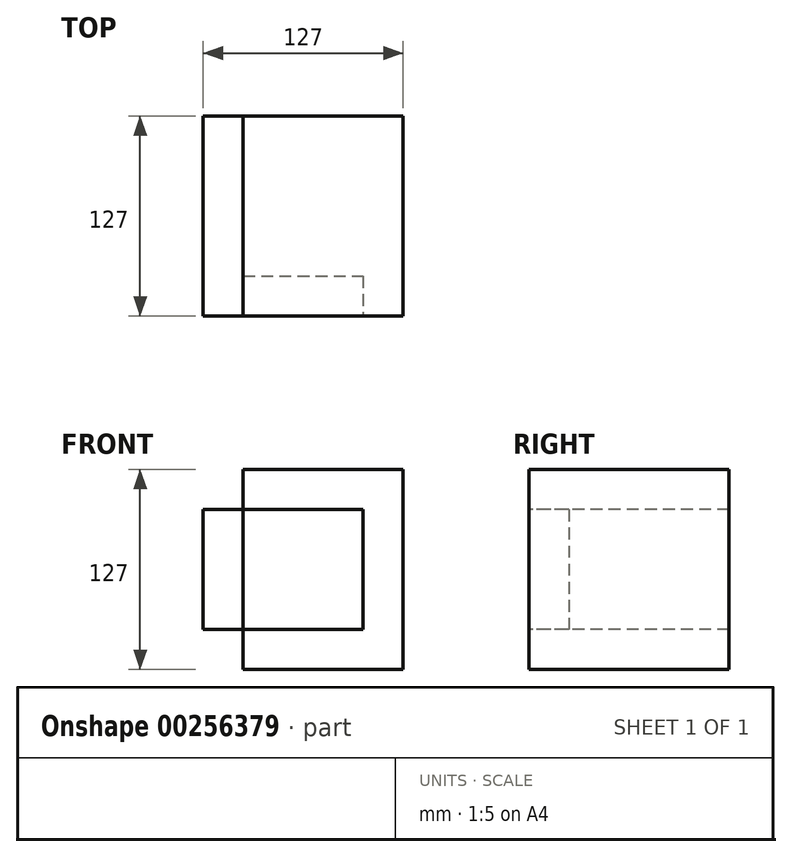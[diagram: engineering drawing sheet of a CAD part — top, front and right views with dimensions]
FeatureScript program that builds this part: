
annotation { "Feature Type Name" : "Feature", "Feature Type Description" : "" }
export const myFeature = defineFeature(function(context is Context, id is Id, definition is map)
    precondition{}
    {
        {
            var Q0;
            Q0=qCreatedBy(makeId("Front.planeOp"),FACE);
            var sketch = newSketch(context, id + "F0", { "sketchPlane" : qUnion([Q0])});
            skLineSegment(sketch, "E0.bottom", {"start": v(63.5, 63.5) * mm, "end": v(-63.5, 63.5) * mm});
            skLineSegment(sketch, "E0.top", {"start": v(63.5, -63.5) * mm, "end": v(-63.5, -63.5) * mm});
            skLineSegment(sketch, "E0.left", {"start": v(63.5, 63.5) * mm, "end": v(63.5, -63.5) * mm});
            skLineSegment(sketch, "E0.right", {"start": v(-63.5, 63.5) * mm, "end": v(-63.5, -63.5) * mm});
            skPoint(sketch, "E0.middle", {"position": v(0, 0) * mm});
            skLineSegment(sketch, "E1.bottom", {"start": v(-40.9, 63.5) * mm, "end": v(-63.5, 63.5) * mm});
            skLineSegment(sketch, "E1.top", {"start": v(-40.9, -63.5) * mm, "end": v(-63.5, -63.5) * mm});
            skLineSegment(sketch, "E2.bottom", {"start": v(-63.5, 63.5) * mm, "end": v(-38.1, 63.5) * mm});
            skLineSegment(sketch, "E2.top", {"start": v(-63.5, -63.5) * mm, "end": v(-38.1, -63.5) * mm});
            skLineSegment(sketch, "E2.right", {"start": v(-38.1, 63.5) * mm, "end": v(-38.1, -63.5) * mm});
            skLineSegment(sketch, "E3.bottom", {"start": v(38.1, 63.5) * mm, "end": v(63.5, 63.5) * mm});
            skLineSegment(sketch, "E3.top", {"start": v(38.1, -63.5) * mm, "end": v(63.5, -63.5) * mm});
            skLineSegment(sketch, "E3.left", {"start": v(38.1, 63.5) * mm, "end": v(38.1, -63.5) * mm});
            skLineSegment(sketch, "E4.bottom", {"start": v(-63.5, 38.1) * mm, "end": v(63.5, 38.1) * mm});
            skLineSegment(sketch, "E4.top", {"start": v(-63.5, 63.5) * mm, "end": v(63.5, 63.5) * mm});
            skLineSegment(sketch, "E4.left", {"start": v(-63.5, 38.1) * mm, "end": v(-63.5, 63.5) * mm});
            skLineSegment(sketch, "E4.right", {"start": v(63.5, 38.1) * mm, "end": v(63.5, 63.5) * mm});
            skLineSegment(sketch, "E5.bottom", {"start": v(-63.5, -38.1) * mm, "end": v(63.5, -38.1) * mm});
            skLineSegment(sketch, "E5.top", {"start": v(-63.5, -63.5) * mm, "end": v(63.5, -63.5) * mm});
            skLineSegment(sketch, "E5.left", {"start": v(-63.5, -38.1) * mm, "end": v(-63.5, -63.5) * mm});
            skLineSegment(sketch, "E5.right", {"start": v(63.5, -38.1) * mm, "end": v(63.5, -63.5) * mm});
            skSolve(sketch);
        }
        {
            var Q0;
            {var subQ5=sQuery(id+"F0.wireOp",EDGE,"E5.left");Q0=makeQuery(id+"F0.imprint","IMPRINT",FACE,{"disambiguationData":[TD([[makeQuery(id+"F0.imprint","IMPRINT",EDGE,{"derivedFrom":subQ5}),1.0]])]});}
            var Q1;
            {var subQ5=sQuery(id+"F0.wireOp",EDGE,"E4.right");Q1=makeQuery(id+"F0.imprint","IMPRINT",FACE,{"disambiguationData":[TD([[makeQuery(id+"F0.imprint","IMPRINT",EDGE,{"derivedFrom":subQ5}),1.0]])]});}
            var Q2;
            {var subQ5=sQuery(id+"F0.wireOp",EDGE,"E5.right");Q2=makeQuery(id+"F0.imprint","IMPRINT",FACE,{"disambiguationData":[TD([[makeQuery(id+"F0.imprint","IMPRINT",EDGE,{"derivedFrom":subQ5}),-1.0]])]});}
            var Q3;
            {var subQ0=sQuery(id+"F0.wireOp",EDGE,"E0.right");Q3=makeQuery(id+"F0.imprint","IMPRINT",FACE,{"disambiguationData":[TD([[makeQuery(id+"F0.imprint","IMPRINT",EDGE,{"derivedFrom":subQ0}),1.0]])]});}
            var Q4;
            {var subQ0=sQuery(id+"F0.wireOp",EDGE,"E5.top");var subQ1=sQuery(id+"F0.wireOp",EDGE,"E2.right");var subQ2=makeQuery(id+"F0.imprint","INTERSECT",VERTEX,{"derivedFrom":[subQ1,subQ0]});Q4=makeQuery(id+"F0.imprint","IMPRINT",FACE,{"disambiguationData":[TD([[makeQuery(id+"F0.imprint","IMPRINT",EDGE,{"disambiguationData":[TD([[subQ2,1.0]])],"derivedFrom":subQ1}),1.0]])]});}
            var Q5;
            {var subQ5=sQuery(id+"F0.wireOp",EDGE,"E0.left");Q5=makeQuery(id+"F0.imprint","IMPRINT",FACE,{"disambiguationData":[TD([[makeQuery(id+"F0.imprint","IMPRINT",EDGE,{"derivedFrom":subQ5}),-1.0]])]});}
            var Q6;
            {var subQ5=sQuery(id+"F0.wireOp",EDGE,"E4.left");Q6=makeQuery(id+"F0.imprint","IMPRINT",FACE,{"disambiguationData":[TD([[makeQuery(id+"F0.imprint","IMPRINT",EDGE,{"derivedFrom":subQ5}),-1.0]])]});}
            var Q7;
            {var subQ0=sQuery(id+"F0.wireOp",EDGE,"E4.top");var subQ1=sQuery(id+"F0.wireOp",EDGE,"E2.right");var subQ2=makeQuery(id+"F0.imprint","INTERSECT",VERTEX,{"derivedFrom":[subQ1,subQ0]});Q7=makeQuery(id+"F0.imprint","IMPRINT",FACE,{"disambiguationData":[TD([[makeQuery(id+"F0.imprint","IMPRINT",EDGE,{"disambiguationData":[TD([[subQ2,-1.0]])],"derivedFrom":subQ1}),1.0]])]});}
            extrude(context, id + "F1", {"entities" : qUnion([Q0, Q1, Q2, Q3, Q4, Q5, Q6, Q7]), "oppositeDirection" : true, "depth" : 127 * mm});
        }
        {
            var Q0;
            {var subQ0=sQuery(id+"F0.wireOp",EDGE,"E4.bottom");var subQ1=sQuery(id+"F0.wireOp",EDGE,"E2.right");var subQ2=makeQuery(id+"F0.imprint","INTERSECT",VERTEX,{"derivedFrom":[subQ1,subQ0]});Q0=makeQuery(id+"F0.imprint","IMPRINT",FACE,{"disambiguationData":[TD([[makeQuery(id+"F0.imprint","IMPRINT",EDGE,{"disambiguationData":[TD([[subQ2,-1.0]])],"derivedFrom":subQ1}),1.0]])]});}
            extrude(context, id + "F2", {"entities" : qUnion([Q0]), "oppositeDirection" : true, "depth" : 25.4 * mm});
        }
    });
